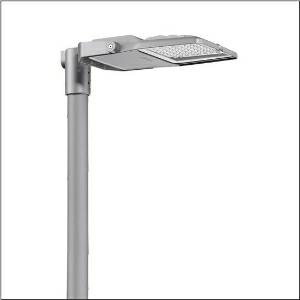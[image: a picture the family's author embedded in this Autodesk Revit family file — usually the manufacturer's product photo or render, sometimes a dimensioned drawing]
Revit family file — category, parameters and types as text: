
# Revit family: floodlight_fl_21_iq_mini___pl52_5xa7771d2d3a_64cb
name_source: partatom
category: Lighting Fixtures
units: mm (PartAtom-declared; Revit-internal decimal feet)

## family parameters
Cut with Voids When Loaded = No
Host = Face
Light Source = No
Part Type = Normal
Room Calculation Point = No
Round Connector Dimension = Use Diameter
Shared = No

## types (1)
- --- (1 x LED, 17830 lm, 143 W, 3000K)
    Apparent Load = 143 VA
    CIE Flux Codes = 26 60 98 100 100
    Color Rendering = 70
    Color Temperature = 3000K
    Default Elevation = 1800 mm
    Description = Floodlight FL 21 iQ mini, floodlight, primary light control with lens, of PMMA, primary optical cover: protective disc, of toughened safety glass, transparent, light distribution: PL52, light emission: direct distribution, installation type: surface-mounted, LED, High Power LED, rated luminous flux: 17.830lm, luminous efficacy: 125lm/W, light colour: 730, colour temperature: 3000K, control gear: iQ Comfort/DALI, control: Auto-Match, Temp-Guard, Lumen-Switch, Night-Set, Smart-Wire, Light-Fading, Desk-Remote (wireless, voltage-free reading and setting of iQ features in the workshop via application-optimized NFC function/RFID function), optimised constant luminous flux control (CLO 2.0), with terminal, 6-pole, mains connection: 220..240V, AC, 50/60Hz, start of lifetime: 143W, end of service life: 152W, reduction: 61W, luminaire housing, of diecast aluminium, powder-coated, Siteco® metallic grey (DB 702S), corrosivity category C5 mid according to DIN EN ISO 12944, suitable for swimming pools, chlorine-resistant, sealing non-destructively replaceable, please order mast flange separately, mast bracket, of steel, galvanised, powder-coated, Siteco® metallic grey (DB 702S), protection rating (complete): IP66, insulation class (complete): insulation class II (safety insulation), certification: CE, ENEC, VDE, protection symbol: D, impact resistance: IK08, permissible operating ambient temperature: -40..+40°C, permissible operating ambient temperature for outdoor applications: -40..+50°C, standard: DIN EN 12944, LABS conformity tested according to VDMA 24364:2018-05, packaging unit: 1 piece

Light Distribution: PL52
    Height = 70 mm
    Lamp = 1 x LED
    Lamp Light Flux = 17830 lm
    Lamp Power = 143 W
    Lamp count = 1
    Length = 485 mm
    Luminous efficacy = 125 lm/W
    Manufacturer = Siteco
    ModVariant = No
    Model = 5XA7771D2D3A
    Number of Poles = 1
    OnlyDefault = Yes
    Power Factor = 1
    Product Name = Floodlight FL 21 iQ mini | PL52
    Product group = floodlight | pylon annexe
    ProductGroupID = 6201
    Protection Class = Protection class II
    Protection Degree = IP 66
    RLX_Detail_Level = 1
    RLX_Emergency_Light_Flux = 0 lm
    RLX_Emergency_Type = 0
    RLX_Emergency_Type_DB = No
    RlxData = <blob elided: 101805 chars, md5=52a4467e>
    Socket = socket
    Standby Power = 0 W
    System Light Flux = 17830 lm
    System Power = 143 W
    Type Comments = factory setting: luminous flux: 100 % | dim-lin: 254 | 730 mA
    Type Image = l_1007125.jpg
    URL = http://relux.com
    VarID = @adj_185435
    Voltage = 0 V
    Weight = 0.00 kg
    Width = 337 mm

## geometry (parser evidence)
native form markers: Blend x4, Sweep x13
no freeform markers — native parametric forms only
